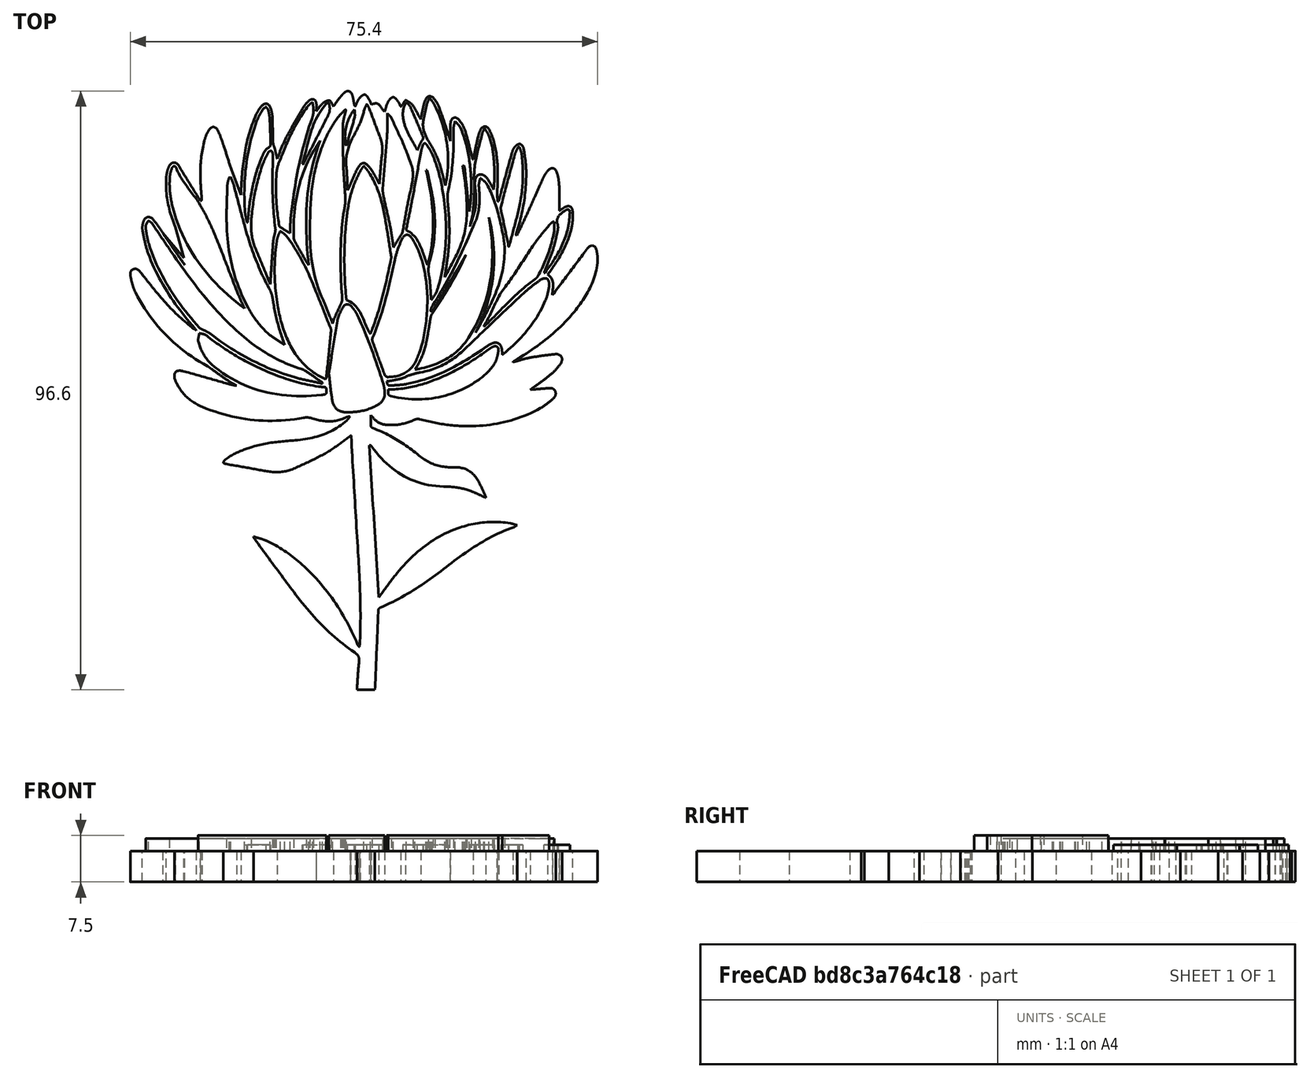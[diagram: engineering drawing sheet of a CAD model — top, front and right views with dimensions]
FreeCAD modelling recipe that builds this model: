
FCSTD DOCUMENT  (FreeCAD 1.0R39109 (Git))
Label: Protea
License: All rights reserved
LicenseURL: https://en.wikipedia.org/wiki/All_rights_reserved
objects: Part::Extrusion×30, Part::Feature×29, Part::MultiFuse×2, Part::Scale×1, Sketcher::SketchObject×1
note: 64 computed .brp shape members not serialized (recipe doc carries the construction recipe); baked Part::Feature solids carry a one-line shape summary decoded from their .brp

FEATURE [Part::Feature] Path003
  shape: bbox 15.25 x 54.21 x 2e-07 mm, 0 faces, 0 solids (baked)
FEATURE [Part::Feature] Path004
  shape: bbox 12.02 x 69.08 x 2e-07 mm, 0 faces, 0 solids (baked)
FEATURE [Part::Feature] Path005
  shape: bbox 17.86 x 46.18 x 2e-07 mm, 0 faces, 0 solids (baked)
FEATURE [Part::Feature] Path006
  shape: bbox 18.44 x 47.75 x 2e-07 mm, 0 faces, 0 solids (baked)
FEATURE [Part::Feature] Path008
  shape: bbox 57.09 x 52.57 x 2e-07 mm, 0 faces, 0 solids (baked)
FEATURE [Part::Feature] Path010
  shape: bbox 18.81 x 54.02 x 2e-07 mm, 0 faces, 0 solids (baked)
FEATURE [Part::Feature] Path011
  shape: bbox 24.33 x 46.03 x 2e-07 mm, 0 faces, 0 solids (baked)
FEATURE [Part::Feature] Path014
  shape: bbox 10.35 x 43.33 x 2e-07 mm, 0 faces, 0 solids (baked)
FEATURE [Part::Feature] Path015
  shape: bbox 41.67 x 20.98 x 2e-07 mm, 0 faces, 0 solids (baked)
FEATURE [Part::Feature] Path017
  shape: bbox 12.3 x 42.22 x 2e-07 mm, 0 faces, 0 solids (baked)
FEATURE [Part::Feature] Path018
  shape: bbox 8.11 x 43.14 x 2e-07 mm, 0 faces, 0 solids (baked)
FEATURE [Part::Feature] Path021
  shape: bbox 11.97 x 27.75 x 2e-07 mm, 0 faces, 0 solids (baked)
FEATURE [Part::Feature] Path026
  shape: bbox 8.764 x 37.3 x 2e-07 mm, 0 faces, 0 solids (baked)
FEATURE [Part::Feature] Path029
  shape: bbox 8.697 x 40.08 x 2e-07 mm, 0 faces, 0 solids (baked)
FEATURE [Part::Feature] Path030
  shape: bbox 8.727 x 28.27 x 2e-07 mm, 0 faces, 0 solids (baked)
FEATURE [Part::Feature] Path027
  shape: bbox 7.258 x 32.17 x 2e-07 mm, 0 faces, 0 solids (baked)
FEATURE [Part::Feature] Path034
  shape: bbox 8.375 x 20.67 x 2e-07 mm, 0 faces, 0 solids (baked)
FEATURE [Part::Feature] Path023
  shape: bbox 22.84 x 33.83 x 2e-07 mm, 0 faces, 0 solids (baked)
FEATURE [Part::Feature] Path012
  shape: bbox 52.55 x 34.76 x 2e-07 mm, 0 faces, 0 solids (baked)
FEATURE [Part::Feature] Path019
  shape: bbox 35.92 x 17.67 x 2e-07 mm, 0 faces, 0 solids (baked)
FEATURE [Part::Feature] Path007
  shape: bbox 18.19 x 35.14 x 2e-07 mm, 0 faces, 0 solids (baked)
FEATURE [Part::Feature] Path
  shape: bbox 151 x 193.3 x 2e-07 mm, 0 faces, 0 solids (baked)
FEATURE [Part::Feature] Path031
  shape: bbox 7.945 x 31.58 x 2e-07 mm, 0 faces, 0 solids (baked)
FEATURE [Part::Feature] Path002
  shape: bbox 29.27 x 61.79 x 2e-07 mm, 0 faces, 0 solids (baked)
FEATURE [Part::Feature] Path016
  shape: bbox 8.658 x 50.28 x 2e-07 mm, 0 faces, 0 solids (baked)
FEATURE [Part::Feature] Path035
  shape: bbox 8.954 x 20.08 x 2e-07 mm, 0 faces, 0 solids (baked)
FEATURE [Part::Feature] Path037
  shape: bbox 3.475 x 11.64 x 2e-07 mm, 0 faces, 0 solids (baked)
FEATURE [Part::Feature] Path033
  shape: bbox 6.727 x 15.52 x 2e-07 mm, 0 faces, 0 solids (baked)
FEATURE [Part::Feature] Path009
  shape: bbox 13.11 x 50.54 x 2e-07 mm, 0 faces, 0 solids (baked)
FEATURE [Part::Extrusion] Extrude
  Base = -> Path
  Dir = (0,0,-1)
  DirMode = 2
  FaceMakerClass = Part::FaceMakerBullseye
  FaceMakerMode = 3
  LengthFwd = 5
  LengthRev = 0
  Solid = true
  Symmetric = false
FEATURE [Part::Extrusion] Extrude001
  Base = -> Path002
  Dir = (0,0,1)
  DirMode = 2
  FaceMakerClass = Part::FaceMakerBullseye
  FaceMakerMode = 3
  LengthFwd = 2
  LengthRev = 0
  Solid = true
  Symmetric = false
FEATURE [Part::Extrusion] Extrude002
  Base = -> Path019
  Dir = (0,0,1)
  DirMode = 2
  FaceMakerClass = Part::FaceMakerBullseye
  FaceMakerMode = 3
  LengthFwd = 2.5
  LengthRev = 0
  Solid = true
  Symmetric = false
FEATURE [Part::Extrusion] Extrude003
  Base = -> Path003
  Dir = (0,0,1)
  DirMode = 2
  FaceMakerClass = Part::FaceMakerBullseye
  FaceMakerMode = 3
  LengthFwd = 2
  LengthRev = 0
  Solid = true
  Symmetric = false
FEATURE [Part::Extrusion] Extrude004
  Base = -> Path004
  Dir = (0,0,1)
  DirMode = 2
  FaceMakerClass = Part::FaceMakerBullseye
  FaceMakerMode = 3
  LengthFwd = 2
  LengthRev = 0
  Solid = true
  Symmetric = false
FEATURE [Part::Extrusion] Extrude005
  Base = -> Path005
  Dir = (0,0,1)
  DirMode = 2
  FaceMakerClass = Part::FaceMakerBullseye
  FaceMakerMode = 3
  LengthFwd = 2
  LengthRev = 0
  Solid = true
  Symmetric = false
FEATURE [Part::Extrusion] Extrude006
  Base = -> Path006
  Dir = (0,0,1)
  DirMode = 2
  FaceMakerClass = Part::FaceMakerBullseye
  FaceMakerMode = 3
  LengthFwd = 2
  LengthRev = 0
  Solid = true
  Symmetric = false
FEATURE [Part::Extrusion] Extrude007
  Base = -> Path007
  Dir = (0,0,1)
  DirMode = 2
  FaceMakerClass = Part::FaceMakerBullseye
  FaceMakerMode = 3
  LengthFwd = 2.5
  LengthRev = 0
  Solid = true
  Symmetric = false
FEATURE [Part::Extrusion] Extrude008
  Base = -> Path008
  Dir = (0,0,1)
  DirMode = 2
  FaceMakerClass = Part::FaceMakerBullseye
  FaceMakerMode = 3
  LengthFwd = 2
  LengthRev = 0
  Solid = true
  Symmetric = false
FEATURE [Part::Extrusion] Extrude009
  Base = -> Path009
  Dir = (0,0,1)
  DirMode = 2
  FaceMakerClass = Part::FaceMakerBullseye
  FaceMakerMode = 3
  LengthFwd = 2
  LengthRev = 0
  Solid = true
  Symmetric = false
FEATURE [Part::Extrusion] Extrude010
  Base = -> Path010
  Dir = (0,0,1)
  DirMode = 2
  FaceMakerClass = Part::FaceMakerBullseye
  FaceMakerMode = 3
  LengthFwd = 2
  LengthRev = 0
  Solid = true
  Symmetric = false
FEATURE [Part::Extrusion] Extrude011
  Base = -> Path011
  Dir = (0,0,1)
  DirMode = 2
  FaceMakerClass = Part::FaceMakerBullseye
  FaceMakerMode = 3
  LengthFwd = 2
  LengthRev = 0
  Solid = true
  Symmetric = false
FEATURE [Part::Extrusion] Extrude012
  Base = -> Path012
  Dir = (0,0,1)
  DirMode = 2
  FaceMakerClass = Part::FaceMakerBullseye
  FaceMakerMode = 3
  LengthFwd = 2.5
  LengthRev = 0
  Solid = true
  Symmetric = false
FEATURE [Part::Extrusion] Extrude013
  Base = -> Path014
  Dir = (0,0,1)
  DirMode = 2
  FaceMakerClass = Part::FaceMakerBullseye
  FaceMakerMode = 3
  LengthFwd = 2
  LengthRev = 0
  Solid = true
  Symmetric = false
FEATURE [Part::Extrusion] Extrude014
  Base = -> Path015
  Dir = (0,0,1)
  DirMode = 2
  FaceMakerClass = Part::FaceMakerBullseye
  FaceMakerMode = 3
  LengthFwd = 2.5
  LengthRev = 0
  Solid = true
  Symmetric = false
FEATURE [Part::Extrusion] Extrude015
  Base = -> Path016
  Dir = (0,0,1)
  DirMode = 2
  FaceMakerClass = Part::FaceMakerBullseye
  FaceMakerMode = 3
  LengthFwd = 2
  LengthRev = 0
  Solid = true
  Symmetric = false
FEATURE [Part::Extrusion] Extrude016
  Base = -> Path017
  Dir = (0,0,1)
  DirMode = 2
  FaceMakerClass = Part::FaceMakerBullseye
  FaceMakerMode = 3
  LengthFwd = 2
  LengthRev = 0
  Solid = true
  Symmetric = false
FEATURE [Part::Extrusion] Extrude017
  Base = -> Path018
  Dir = (0,0,1)
  DirMode = 2
  FaceMakerClass = Part::FaceMakerBullseye
  FaceMakerMode = 3
  LengthFwd = 2
  LengthRev = 0
  Solid = true
  Symmetric = false
FEATURE [Part::Extrusion] Extrude018
  Base = -> Path021
  Dir = (0,0,1)
  DirMode = 2
  FaceMakerClass = Part::FaceMakerBullseye
  FaceMakerMode = 3
  LengthFwd = 1
  LengthRev = 0
  Solid = true
  Symmetric = false
FEATURE [Part::Extrusion] Extrude019
  Base = -> Path023
  Dir = (0,0,1)
  DirMode = 2
  FaceMakerClass = Part::FaceMakerBullseye
  FaceMakerMode = 3
  LengthFwd = 2
  LengthRev = 0
  Solid = true
  Symmetric = false
FEATURE [Part::Extrusion] Extrude020
  Base = -> Path029
  Dir = (0,0,1)
  DirMode = 2
  FaceMakerClass = Part::FaceMakerBullseye
  FaceMakerMode = 3
  LengthFwd = 2
  LengthRev = 0
  Solid = true
  Symmetric = false
FEATURE [Part::Extrusion] Extrude021
  Base = -> Path030
  Dir = (0,0,1)
  DirMode = 2
  FaceMakerClass = Part::FaceMakerBullseye
  FaceMakerMode = 3
  LengthFwd = 1
  LengthRev = 0
  Solid = true
  Symmetric = false
FEATURE [Part::Extrusion] Extrude022
  Base = -> Path033
  Dir = (0,0,1)
  DirMode = 2
  FaceMakerClass = Part::FaceMakerBullseye
  FaceMakerMode = 3
  LengthFwd = 1
  LengthRev = 0
  Solid = true
  Symmetric = false
FEATURE [Part::Extrusion] Extrude023
  Base = -> Path034
  Dir = (0,0,1)
  DirMode = 2
  FaceMakerClass = Part::FaceMakerBullseye
  FaceMakerMode = 3
  LengthFwd = 1
  LengthRev = 0
  Solid = true
  Symmetric = false
FEATURE [Part::Extrusion] Extrude024
  Base = -> Path035
  Dir = (0,0,1)
  DirMode = 2
  FaceMakerClass = Part::FaceMakerBullseye
  FaceMakerMode = 3
  LengthFwd = 1
  LengthRev = 0
  Solid = true
  Symmetric = false
FEATURE [Part::Extrusion] Extrude025
  Base = -> Path026
  Dir = (0,0,1)
  DirMode = 2
  FaceMakerClass = Part::FaceMakerBullseye
  FaceMakerMode = 3
  LengthFwd = 1
  LengthRev = 0
  Solid = true
  Symmetric = false
FEATURE [Part::Extrusion] Extrude026
  Base = -> Path027
  Dir = (0,0,1)
  DirMode = 2
  FaceMakerClass = Part::FaceMakerBullseye
  FaceMakerMode = 3
  LengthFwd = 1
  LengthRev = 0
  Solid = true
  Symmetric = false
FEATURE [Part::Extrusion] Extrude027
  Base = -> Path031
  Dir = (0,0,1)
  DirMode = 2
  FaceMakerClass = Part::FaceMakerBullseye
  FaceMakerMode = 3
  LengthFwd = 1
  LengthRev = 0
  Solid = true
  Symmetric = false
FEATURE [Part::Extrusion] Extrude028
  Base = -> Path037
  Dir = (0,0,1)
  DirMode = 2
  FaceMakerClass = Part::FaceMakerBullseye
  FaceMakerMode = 3
  LengthFwd = 1
  LengthRev = 0
  Solid = true
  Symmetric = false
FEATURE [Part::MultiFuse] Fusion
  Shapes = -> [Extrude,Extrude001,Extrude002,Extrude003,Extrude004,Extrude005,Extrude006,Extrude007,Extrude008,Extrude009,Extrude010,Extrude011,Extrude012,Extrude013,Extrude014,Extrude015,Extrude016,Extrude017,Extrude018,Extrude019,Extrude020,Extrude021,Extrude022,Extrude023,Extrude024,Extrude025,Extrude026,Extrude027,Extrude028]
FEATURE [Part::Scale] Scale
  Base = -> Fusion
  Uniform = false
  UniformScale = 1
  XScale = 0.5
  YScale = 0.5
  ZScale = 1
FEATURE [Sketcher::SketchObject] Sketch
  ArcFitTolerance = 1e-06
  ExternalGeometry = -> [Scale]
  FullyConstrained = false
  MakeInternals = false
  sketch-geometry (6):
    g0: LineSegment StartX=8.103 StartY=-28.2912 StartZ=0 EndX=21.7005 EndY=-47.9796 EndZ=0
    g1: LineSegment StartX=21.7005 StartY=-47.9796 StartZ=0 EndX=30.7156 EndY=-49.77 EndZ=0
    g2: LineSegment StartX=30.7156 StartY=-49.77 StartZ=0 EndX=31.0796 EndY=-47.8936 EndZ=0
    g3: LineSegment StartX=31.0796 StartY=-47.8936 StartZ=0 EndX=10.1473 EndY=-27.3766 EndZ=0
    g4: LineSegment StartX=8.103 StartY=-28.2912 StartZ=0 EndX=11.554 EndY=-32.3919 EndZ=0
    g5: LineSegment StartX=11.554 StartY=-32.3919 StartZ=0 EndX=10.1473 EndY=-27.3766 EndZ=0
  constraints (8):
    c: Coincident(g1,g0)
    c: Coincident(g2,g1)
    c: Coincident(g3,g2)
    c: Coincident(g-4,g0)
    c: Coincident(g-3,g3)
    c: Coincident(g4,g0)
    c: Coincident(g5,g4)
    c: Coincident(g5,g3)
FEATURE [Part::Extrusion] Extrude029
  Base = -> Sketch
  Dir = (0,0,1)
  DirMode = 2
  FaceMakerClass = Part::FaceMakerBullseye
  FaceMakerMode = 3
  LengthFwd = 0
  LengthRev = 5
  Solid = true
  Symmetric = false
FEATURE [Part::MultiFuse] Fusion001
  Shapes = -> [Scale,Extrude029]
